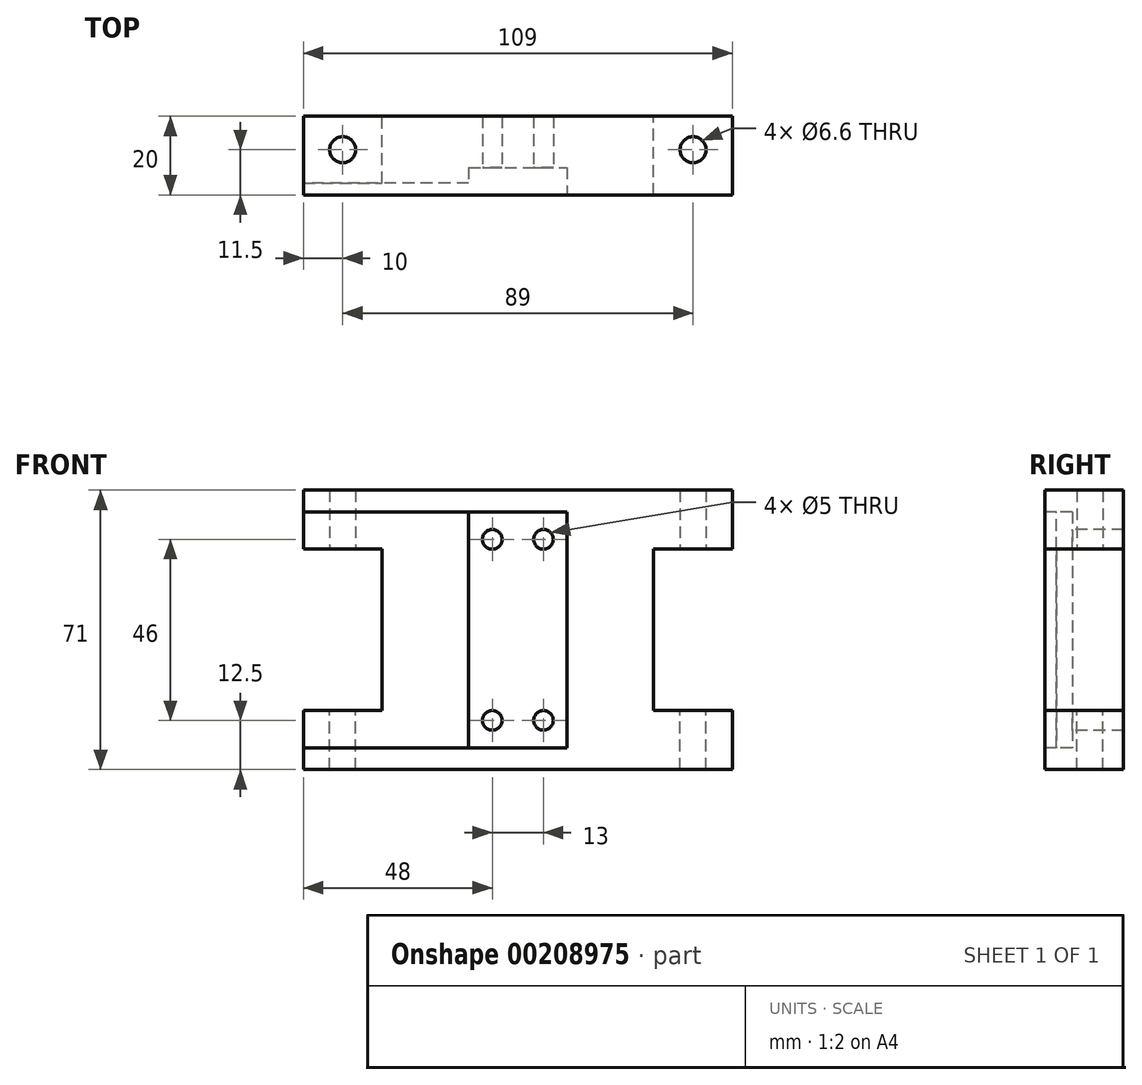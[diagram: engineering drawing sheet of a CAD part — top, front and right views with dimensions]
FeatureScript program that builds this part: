
annotation { "Feature Type Name" : "Feature", "Feature Type Description" : "" }
export const myFeature = defineFeature(function(context is Context, id is Id, definition is map)
    precondition{}
    {
        {
            var Q0;
            Q0=qCreatedBy(makeId("Front.planeOp"),FACE);
            var sketch = newSketch(context, id + "F0", { "sketchPlane" : qUnion([Q0])});
            skLineSegment(sketch, "E0.bottom", {"start": v(-54.5, 35.5) * mm, "end": v(54.5, 35.5) * mm});
            skLineSegment(sketch, "E0.top", {"start": v(-54.5, -35.5) * mm, "end": v(54.5, -35.5) * mm});
            skLineSegment(sketch, "E1", {"start": v(-54.5, 0) * mm, "end": v(54.5, 0) * mm, "construction": true});
            skLineSegment(sketch, "E2", {"start": v(0, 35.5) * mm, "end": v(0, -35.5) * mm, "construction": true});
            skLineSegment(sketch, "E3", {"start": v(54.5, 20.5) * mm, "end": v(34.5, 20.5) * mm});
            skLineSegment(sketch, "E4", {"start": v(34.5, 20.5) * mm, "end": v(34.5, 0) * mm});
            skLineSegment(sketch, "E5.MirrorCS", {"start": v(34.5, -20.5) * mm, "end": v(34.5, 0) * mm});
            skLineSegment(sketch, "E6.MirrorCS", {"start": v(54.5, -20.5) * mm, "end": v(34.5, -20.5) * mm});
            skLineSegment(sketch, "E7.MirrorCS", {"start": v(-34.5, 20.5) * mm, "end": v(-34.5, 0) * mm});
            skLineSegment(sketch, "E8.MirrorCS", {"start": v(-54.5, 20.5) * mm, "end": v(-34.5, 20.5) * mm});
            skLineSegment(sketch, "E9.MirrorCS", {"start": v(-34.5, -20.5) * mm, "end": v(-34.5, 0) * mm});
            skLineSegment(sketch, "E10.MirrorCS", {"start": v(-54.5, -20.5) * mm, "end": v(-34.5, -20.5) * mm});
            skLineSegment(sketch, "E11.trimOffspring", {"start": v(54.5, -20.5) * mm, "end": v(54.5, -35.5) * mm});
            skLineSegment(sketch, "E12", {"start": v(-54.5, 20.5) * mm, "end": v(-54.5, 35.5) * mm});
            skLineSegment(sketch, "E13", {"start": v(54.5, 20.5) * mm, "end": v(54.5, 35.5) * mm});
            skLineSegment(sketch, "E14", {"start": v(-54.5, -20.5) * mm, "end": v(-54.5, -35.5) * mm});
            skSolve(sketch);
        }
        {
            var Q0;
            Q0=makeQuery(id+"F0.imprint","IMPRINT",FACE,{"disambiguationData":[TD([[makeQuery(id+"F0.imprint","IMPRINT",EDGE,{"derivedFrom":sQuery(id+"F0.wireOp",EDGE,"E0.bottom")}),-1.0]])]});
            extrude(context, id + "F1", {"entities" : qUnion([Q0]), "depth" : 20 * mm});
        }
        {
            var Q0;
            Q0=makeQuery(id+"F1.opExtrude","CAP_FACE",FACE,{"disambiguationData":[OSD([sQuery(id+"F0.wireOp",EDGE,"E0.bottom"),sQuery(id+"F0.wireOp",EDGE,"E0.top"),sQuery(id+"F0.wireOp",EDGE,"E3"),sQuery(id+"F0.wireOp",EDGE,"E4"),sQuery(id+"F0.wireOp",EDGE,"E5.MirrorCS"),sQuery(id+"F0.wireOp",EDGE,"E6.MirrorCS"),sQuery(id+"F0.wireOp",EDGE,"E7.MirrorCS"),sQuery(id+"F0.wireOp",EDGE,"E8.MirrorCS"),sQuery(id+"F0.wireOp",EDGE,"E9.MirrorCS"),sQuery(id+"F0.wireOp",EDGE,"E10.MirrorCS"),sQuery(id+"F0.wireOp",EDGE,"E11.trimOffspring"),sQuery(id+"F0.wireOp",EDGE,"E12"),sQuery(id+"F0.wireOp",EDGE,"E13"),sQuery(id+"F0.wireOp",EDGE,"E14")])],"isStart":false});
            var sketch = newSketch(context, id + "F2", { "sketchPlane" : qUnion([Q0])});
            skLineSegment(sketch, "E15", {"start": v(-34.5, 0) * mm, "end": v(-12.5, 0) * mm, "construction": true});
            skLineSegment(sketch, "E16", {"start": v(0, 35.5) * mm, "end": v(0, 30) * mm, "construction": true});
            skLineSegment(sketch, "E17.bottom", {"start": v(-12.5, 30) * mm, "end": v(0, 30) * mm});
            skLineSegment(sketch, "E17.left", {"start": v(-12.5, 30) * mm, "end": v(-12.5, 0) * mm});
            skLineSegment(sketch, "E18.MirrorCS", {"start": v(12.5, 30) * mm, "end": v(0, 30) * mm});
            skLineSegment(sketch, "E19.MirrorCS", {"start": v(12.5, 30) * mm, "end": v(12.5, 0) * mm});
            skLineSegment(sketch, "E20.MirrorCS", {"start": v(12.5, -30) * mm, "end": v(0, -30) * mm});
            skLineSegment(sketch, "E21.MirrorCS", {"start": v(-12.5, -30) * mm, "end": v(0, -30) * mm});
            skLineSegment(sketch, "E22.MirrorCS", {"start": v(-12.5, -30) * mm, "end": v(-12.5, 0) * mm});
            skLineSegment(sketch, "E23.MirrorCS", {"start": v(12.5, -30) * mm, "end": v(12.5, 0) * mm});
            skLineSegment(sketch, "E24.trimOffspring", {"start": v(0, -30) * mm, "end": v(0, -35.5) * mm, "construction": true});
            skLineSegment(sketch, "E25.trimOffspring", {"start": v(12.5, 0) * mm, "end": v(34.5, 0) * mm, "construction": true});
            skPoint(sketch, "E17.top.end.orphan", {"position": v(0, 0) * mm});
            skLineSegment(sketch, "E26", {"start": v(-12.5, -30) * mm, "end": v(-54.5, -30) * mm});
            skLineSegment(sketch, "E27.MirrorCS", {"start": v(-12.5, 30) * mm, "end": v(-54.5, 30) * mm});
            skPoint(sketch, "E28", {"position": v(0, 23) * mm});
            skPoint(sketch, "E29", {"position": v(0, -23) * mm});
            skPoint(sketch, "E30", {"position": v(-6.5, 23) * mm});
            skPoint(sketch, "E31", {"position": v(6.5, 23) * mm});
            skPoint(sketch, "E32", {"position": v(-6.5, -23) * mm});
            skPoint(sketch, "E33", {"position": v(6.5, -23) * mm});
            skSolve(sketch);
        }
        {
            var Q0;
            Q0=makeQuery(id+"F2.imprint","IMPRINT",FACE,{"disambiguationData":[TD([[makeQuery(id+"F2.imprint","IMPRINT",EDGE,{"derivedFrom":sQuery(id+"F2.wireOp",EDGE,"E17.bottom")}),-1.0]])]});
            extrude(context, id + "F3", {"entities" : qUnion([Q0]), "operationType" : NewBodyOperationType.REMOVE, "oppositeDirection" : true, "depth" : 7 * mm});
        }
        {
            var Q0;
            Q0=makeQuery(id+"F2.imprint","IMPRINT",FACE,{"disambiguationData":[TD([[makeQuery(id+"F2.imprint","IMPRINT",EDGE,{"derivedFrom":sQuery(id+"F2.wireOp",EDGE,"E17.left")}),-1.0]])]});
            extrude(context, id + "F4", {"entities" : qUnion([Q0]), "operationType" : NewBodyOperationType.REMOVE, "oppositeDirection" : true, "depth" : 3 * mm});
        }
        {
            var Q0;
            Q0=makeQuery(id+"F1.opExtrude","SWEPT_FACE",FACE,{"disambiguationData":[OSD([sQuery(id+"F0.wireOp",EDGE,"E8.MirrorCS")])]});
            var sketch = newSketch(context, id + "F5", { "sketchPlane" : qUnion([Q0])});
            skLineSegment(sketch, "E34", {"start": v(-44.5, 17) * mm, "end": v(-44.5, 0) * mm, "construction": true});
            skLineSegment(sketch, "E35", {"start": v(-54.5, 8.5) * mm, "end": v(-34.5, 8.5) * mm, "construction": true});
            skPoint(sketch, "E36", {"position": v(-44.5, 8.5) * mm});
            skPoint(sketch, "E37.MirrorP", {"position": v(44.5, 8.5) * mm});
            skSolve(sketch);
        }
        {
            var Q0;
            Q0=sQuery(id+"F5.wireOp",VERTEX,"E36");
            var Q1;
            Q1=sQuery(id+"F5.wireOp",VERTEX,"E37.MirrorP");
            var Q2;
            Q2=makeQuery(id+"F1.opExtrude","SWEPT_BODY",BODY,{"disambiguationData":[OSD([sQuery(id+"F0.wireOp",EDGE,"E0.bottom"),sQuery(id+"F0.wireOp",EDGE,"E0.top"),sQuery(id+"F0.wireOp",EDGE,"E3"),sQuery(id+"F0.wireOp",EDGE,"E4"),sQuery(id+"F0.wireOp",EDGE,"E5.MirrorCS"),sQuery(id+"F0.wireOp",EDGE,"E6.MirrorCS"),sQuery(id+"F0.wireOp",EDGE,"E7.MirrorCS"),sQuery(id+"F0.wireOp",EDGE,"E8.MirrorCS"),sQuery(id+"F0.wireOp",EDGE,"E9.MirrorCS"),sQuery(id+"F0.wireOp",EDGE,"E10.MirrorCS"),sQuery(id+"F0.wireOp",EDGE,"E11.trimOffspring"),sQuery(id+"F0.wireOp",EDGE,"E12"),sQuery(id+"F0.wireOp",EDGE,"E13"),sQuery(id+"F0.wireOp",EDGE,"E14")])]});
            hole(context, id + "F6", {"style" : HoleStyle.SIMPLE, "endStyle" : HoleEndStyle.THROUGH, "standardTappedOrClearance" : lookupTablePath({ "standard" : "ISO", "fit" : "Normal", "size" : "M6", "type" : "Clearance" }), "standardBlindInLast" : lookupTablePath({ "fit" : "Standard", "standard" : "ISO", "size" : "M6", "type" : "Clearance" }), "holeDiameter" : 6.6 * mm, "locations" : qUnion([Q0, Q1]), "scope" : qUnion([Q2]), "isTappedThrough" : true});
        }
        {
            var Q0;
            Q0=makeQuery(id+"F1.opExtrude","SWEPT_FACE",FACE,{"disambiguationData":[OSD([sQuery(id+"F0.wireOp",EDGE,"E10.MirrorCS")])]});
            var sketch = newSketch(context, id + "F7", { "sketchPlane" : qUnion([Q0])});
            skLineSegment(sketch, "E38", {"start": v(-44.5, 0) * mm, "end": v(-44.5, -17) * mm, "construction": true});
            skLineSegment(sketch, "E39", {"start": v(-54.5, -8.5) * mm, "end": v(-34.5, -8.5) * mm, "construction": true});
            skPoint(sketch, "E40", {"position": v(-44.5, -8.5) * mm});
            skPoint(sketch, "E41.MirrorP", {"position": v(44.5, -8.5) * mm});
            skSolve(sketch);
        }
        {
            var Q0;
            Q0=sQuery(id+"F7.wireOp",VERTEX,"E40");
            var Q1;
            Q1=sQuery(id+"F7.wireOp",VERTEX,"E41.MirrorP");
            var Q2;
            Q2=makeQuery(id+"F1.opExtrude","SWEPT_BODY",BODY,{"disambiguationData":[OSD([sQuery(id+"F0.wireOp",EDGE,"E0.bottom"),sQuery(id+"F0.wireOp",EDGE,"E0.top"),sQuery(id+"F0.wireOp",EDGE,"E3"),sQuery(id+"F0.wireOp",EDGE,"E4"),sQuery(id+"F0.wireOp",EDGE,"E5.MirrorCS"),sQuery(id+"F0.wireOp",EDGE,"E6.MirrorCS"),sQuery(id+"F0.wireOp",EDGE,"E7.MirrorCS"),sQuery(id+"F0.wireOp",EDGE,"E8.MirrorCS"),sQuery(id+"F0.wireOp",EDGE,"E9.MirrorCS"),sQuery(id+"F0.wireOp",EDGE,"E10.MirrorCS"),sQuery(id+"F0.wireOp",EDGE,"E11.trimOffspring"),sQuery(id+"F0.wireOp",EDGE,"E12"),sQuery(id+"F0.wireOp",EDGE,"E13"),sQuery(id+"F0.wireOp",EDGE,"E14")])]});
            hole(context, id + "F8", {"style" : HoleStyle.SIMPLE, "endStyle" : HoleEndStyle.THROUGH, "standardTappedOrClearance" : lookupTablePath({ "standard" : "ISO", "fit" : "Normal", "size" : "M6", "type" : "Clearance" }), "standardBlindInLast" : lookupTablePath({ "fit" : "Standard", "standard" : "ISO", "size" : "M6", "type" : "Clearance" }), "holeDiameter" : 6.6 * mm, "locations" : qUnion([Q0, Q1]), "scope" : qUnion([Q2]), "isTappedThrough" : true});
        }
        {
            var Q0;
            Q0=sQuery(id+"F2.wireOp",VERTEX,"E30");
            var Q1;
            Q1=sQuery(id+"F2.wireOp",VERTEX,"E32");
            var Q2;
            Q2=sQuery(id+"F2.wireOp",VERTEX,"E33");
            var Q3;
            Q3=sQuery(id+"F2.wireOp",VERTEX,"E31");
            var Q4;
            Q4=makeQuery(id+"F1.opExtrude","SWEPT_BODY",BODY,{"disambiguationData":[OSD([sQuery(id+"F0.wireOp",EDGE,"E0.bottom"),sQuery(id+"F0.wireOp",EDGE,"E0.top"),sQuery(id+"F0.wireOp",EDGE,"E3"),sQuery(id+"F0.wireOp",EDGE,"E4"),sQuery(id+"F0.wireOp",EDGE,"E5.MirrorCS"),sQuery(id+"F0.wireOp",EDGE,"E6.MirrorCS"),sQuery(id+"F0.wireOp",EDGE,"E7.MirrorCS"),sQuery(id+"F0.wireOp",EDGE,"E8.MirrorCS"),sQuery(id+"F0.wireOp",EDGE,"E9.MirrorCS"),sQuery(id+"F0.wireOp",EDGE,"E10.MirrorCS"),sQuery(id+"F0.wireOp",EDGE,"E11.trimOffspring"),sQuery(id+"F0.wireOp",EDGE,"E12"),sQuery(id+"F0.wireOp",EDGE,"E13"),sQuery(id+"F0.wireOp",EDGE,"E14")])]});
            hole(context, id + "F9", {"style" : HoleStyle.SIMPLE, "endStyle" : HoleEndStyle.THROUGH, "standardTappedOrClearance" : lookupTablePath({ "standard" : "ISO", "engagement" : "75%", "pitch" : "1 mm", "size" : "M6", "type" : "Tapped" }), "standardBlindInLast" : lookupTablePath({ "standard" : "ISO", "engagement" : "75%", "pitch" : "1 mm", "size" : "M6", "type" : "Tapped" }), "holeDiameter" : 5 * mm, "locations" : qUnion([Q0, Q1, Q2, Q3]), "scope" : qUnion([Q4]), "isTappedThrough" : true, "majorDiameter" : 6 * mm, "showTappedDepth" : true});
        }
    });
